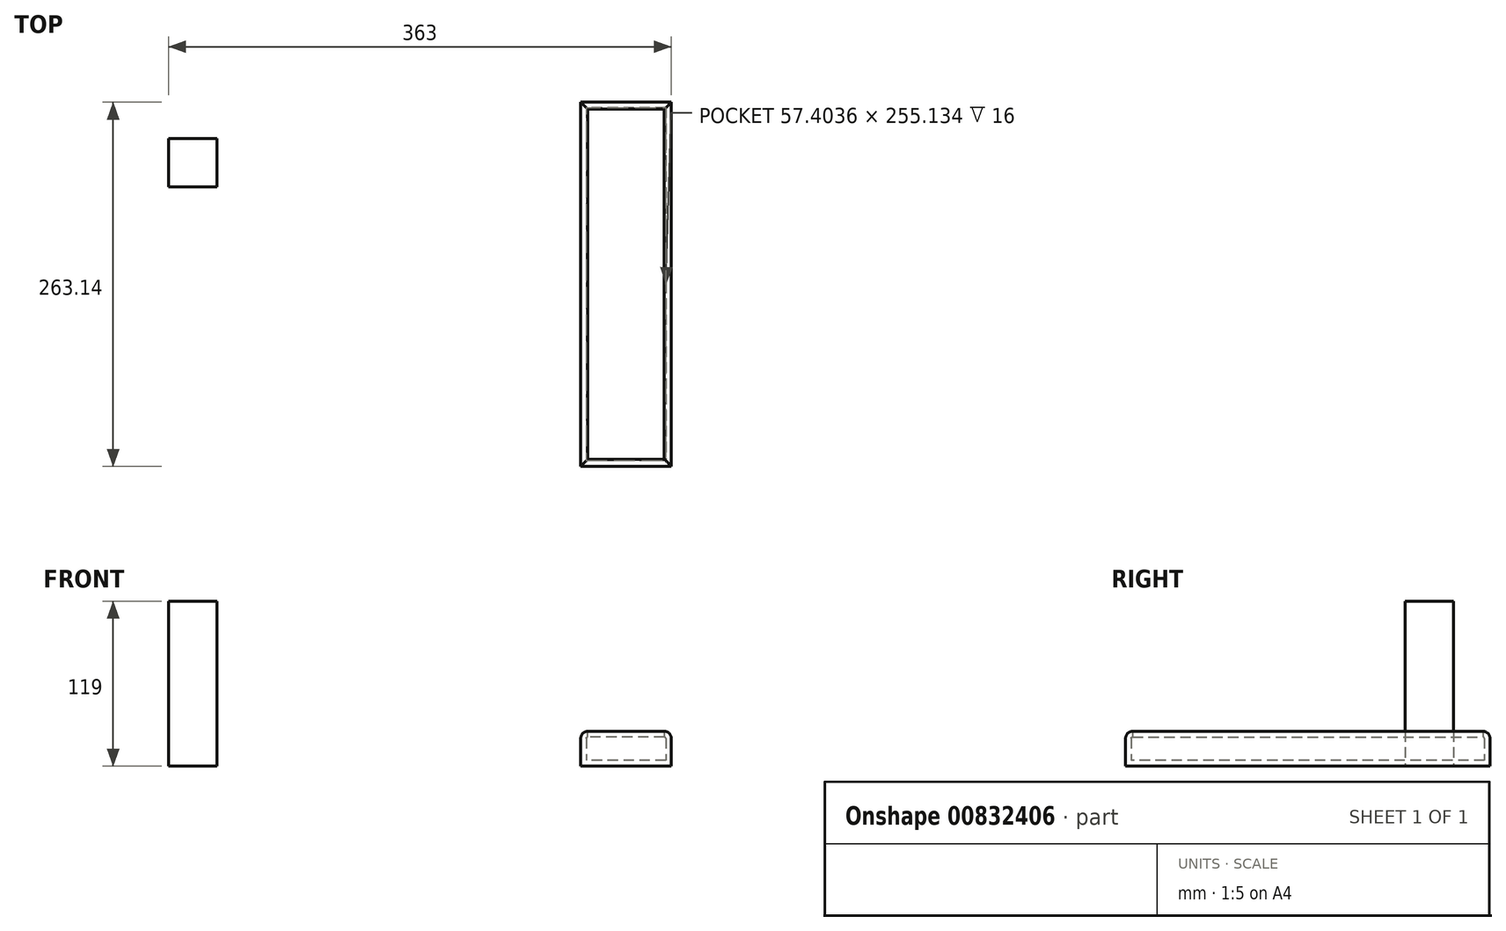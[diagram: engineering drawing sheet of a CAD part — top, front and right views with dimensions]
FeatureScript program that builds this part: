
annotation { "Feature Type Name" : "Feature", "Feature Type Description" : "" }
export const myFeature = defineFeature(function(context is Context, id is Id, definition is map)
    precondition{}
    {
        {
            var Q0;
            Q0=qCreatedBy(makeId("Top.planeOp"),FACE);
            var sketch = newSketch(context, id + "F0", { "sketchPlane" : qUnion([Q0])});
            skLineSegment(sketch, "E0.bottom", {"start": v(-118.71, 73.53) * mm, "end": v(-184.12, 73.53) * mm});
            skLineSegment(sketch, "E0.top", {"start": v(-118.71, -189.6) * mm, "end": v(-184.12, -189.6) * mm});
            skLineSegment(sketch, "E0.left", {"start": v(-118.71, 73.53) * mm, "end": v(-118.71, -189.6) * mm});
            skLineSegment(sketch, "E0.right", {"start": v(-184.12, 73.53) * mm, "end": v(-184.12, -189.6) * mm});
            skPoint(sketch, "E0.middle", {"position": v(-151.42, -58.04) * mm});
            skSolve(sketch);
        }
        {
            var Q0;
            Q0 = qSketchRegion(id + "F0", true);
            extrude(context, id + "F1", {"entities" : qUnion([Q0]), "depth" : 25 * mm, "offsetDistance" : 25 * mm});
        }
        {
            var Q0;
            Q0=makeQuery(id+"F1.opExtrude","CAP_EDGE",EDGE,{"disambiguationData":[OSD([sQuery(id+"F0.wireOp",EDGE,"E0.right")])],"isStart":false});
            var Q1;
            Q1=makeQuery(id+"F1.opExtrude","CAP_EDGE",EDGE,{"disambiguationData":[OSD([sQuery(id+"F0.wireOp",EDGE,"E0.top")])],"isStart":false});
            var Q2;
            Q2=makeQuery(id+"F1.opExtrude","CAP_EDGE",EDGE,{"disambiguationData":[OSD([sQuery(id+"F0.wireOp",EDGE,"E0.left")])],"isStart":false});
            var Q3;
            Q3=makeQuery(id+"F1.opExtrude","CAP_EDGE",EDGE,{"disambiguationData":[OSD([sQuery(id+"F0.wireOp",EDGE,"E0.bottom")])],"isStart":false});
            fillet(context, id + "F2", {"entities" : qUnion([Q0, Q1, Q2, Q3]), "radius" : 5 * mm, "tangentPropagation" : true, "allowEdgeOverflow" : false});
        }
        {
            var Q0;
            Q0=makeQuery(id+"F1.opExtrude","CAP_FACE",FACE,{"disambiguationData":[OSD([sQuery(id+"F0.wireOp",EDGE,"E0.bottom"),sQuery(id+"F0.wireOp",EDGE,"E0.top"),sQuery(id+"F0.wireOp",EDGE,"E0.left"),sQuery(id+"F0.wireOp",EDGE,"E0.right")])],"isStart":false});
            shell(context, id + "F3", {"entities" : qUnion([Q0]), "thickness" : 4 * mm});
        }
        {
            var Q0;
            Q0=qCreatedBy(makeId("Top.planeOp"),FACE);
            var sketch = newSketch(context, id + "F4", { "sketchPlane" : qUnion([Q0])});
            skLineSegment(sketch, "E1.bottom", {"start": v(-446.71, 47.3) * mm, "end": v(-481.71, 47.3) * mm});
            skLineSegment(sketch, "E1.top", {"start": v(-446.71, 12.3) * mm, "end": v(-481.71, 12.3) * mm});
            skLineSegment(sketch, "E1.left", {"start": v(-446.71, 47.3) * mm, "end": v(-446.71, 12.3) * mm});
            skLineSegment(sketch, "E1.right", {"start": v(-481.71, 47.3) * mm, "end": v(-481.71, 12.3) * mm});
            skSolve(sketch);
        }
        {
            var Q0;
            Q0=makeQuery(id+"F4.imprint","IMPRINT",FACE,{"disambiguationData":[TD([[makeQuery(id+"F4.imprint","IMPRINT",EDGE,{"derivedFrom":sQuery(id+"F4.wireOp",EDGE,"E1.bottom")}),1.0]])]});
            extrude(context, id + "F5", {"entities" : qUnion([Q0]), "depth" : 119 * mm, "offsetDistance" : 25 * mm});
        }
    });
